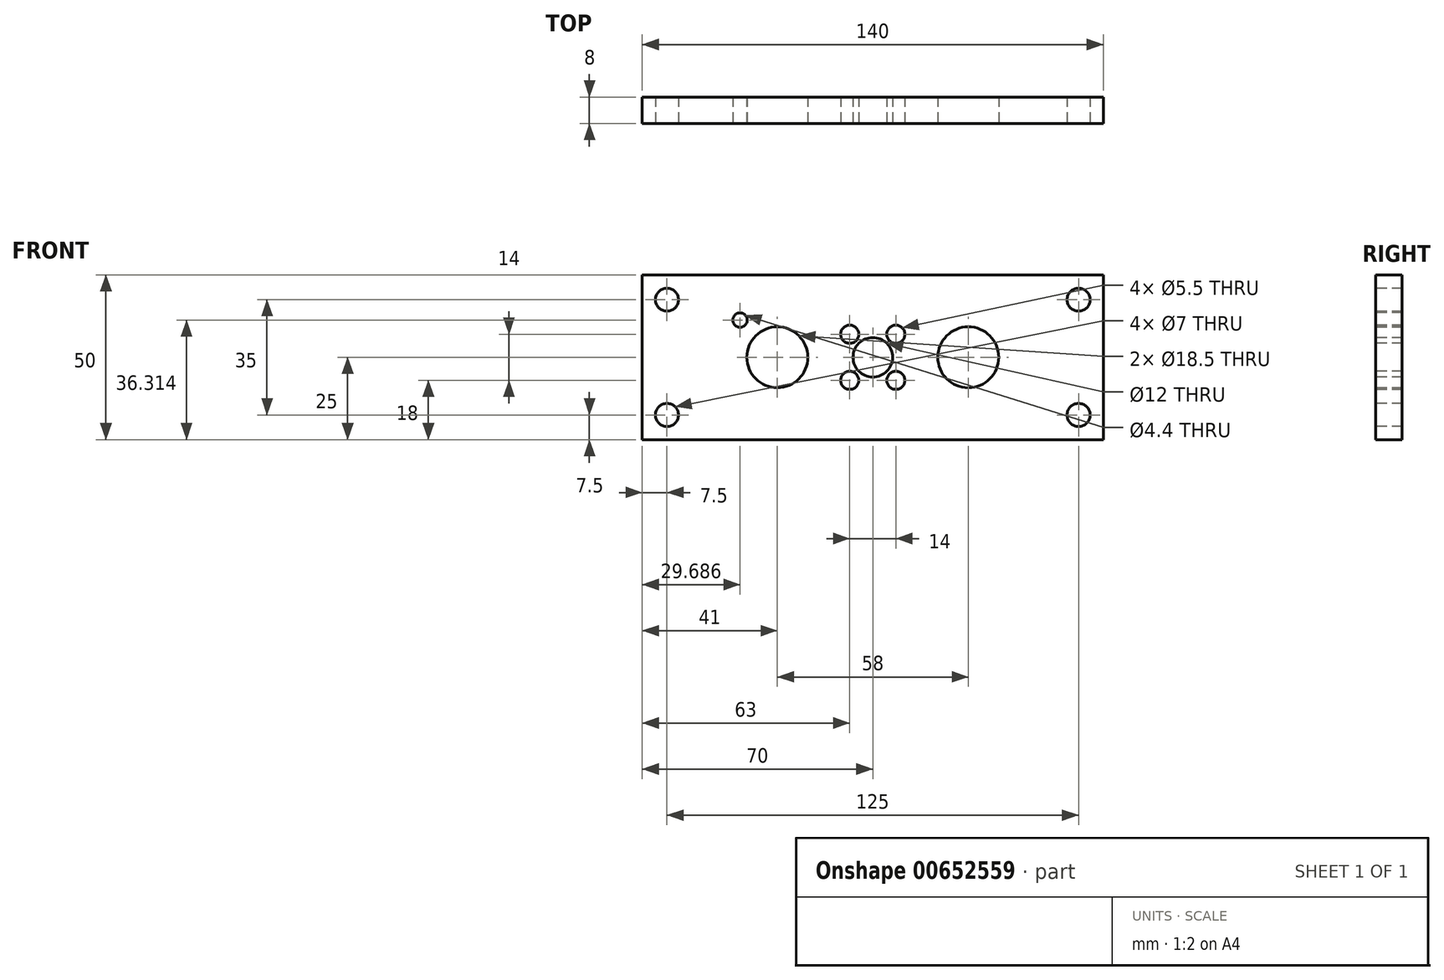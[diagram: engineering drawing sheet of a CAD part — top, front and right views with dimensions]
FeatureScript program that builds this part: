
annotation { "Feature Type Name" : "Feature", "Feature Type Description" : "" }
export const myFeature = defineFeature(function(context is Context, id is Id, definition is map)
    precondition{}
    {
        {
            var Q0;
            Q0=qCreatedBy(makeId("Front.planeOp"),FACE);
            var sketch = newSketch(context, id + "F0", { "sketchPlane" : qUnion([Q0])});
            skLineSegment(sketch, "E0.bottom", {"start": v(70, 25) * mm, "end": v(-70, 25) * mm});
            skLineSegment(sketch, "E0.top", {"start": v(70, -25) * mm, "end": v(-70, -25) * mm});
            skLineSegment(sketch, "E0.left", {"start": v(70, 25) * mm, "end": v(70, -25) * mm});
            skLineSegment(sketch, "E0.right", {"start": v(-70, 25) * mm, "end": v(-70, -25) * mm});
            skPoint(sketch, "E0.middle", {"position": v(0, 0) * mm});
            skSolve(sketch);
        }
        {
            var Q0;
            Q0=makeQuery(id+"F0.imprint","IMPRINT",FACE,{"disambiguationData":[TD([[makeQuery(id+"F0.imprint","IMPRINT",EDGE,{"derivedFrom":sQuery(id+"F0.wireOp",EDGE,"E0.bottom")}),1.0]])]});
            extrude(context, id + "F1", {"entities" : qUnion([Q0]), "depth" : 8 * mm, "offsetDistance" : 25 * mm});
        }
        {
            var Q0;
            Q0=makeQuery(id+"F1.opExtrude","CAP_FACE",FACE,{"disambiguationData":[OSD([sQuery(id+"F0.wireOp",EDGE,"E0.bottom"),sQuery(id+"F0.wireOp",EDGE,"E0.top"),sQuery(id+"F0.wireOp",EDGE,"E0.left"),sQuery(id+"F0.wireOp",EDGE,"E0.right")])],"isStart":false});
            var sketch = newSketch(context, id + "F2", { "sketchPlane" : qUnion([Q0])});
            skPoint(sketch, "E1", {"position": v(-62.5, 17.5) * mm});
            skPoint(sketch, "E2", {"position": v(-62.5, -17.5) * mm});
            skPoint(sketch, "E3", {"position": v(62.5, 17.5) * mm});
            skPoint(sketch, "E4", {"position": v(62.5, -17.5) * mm});
            skPoint(sketch, "E5", {"position": v(-29, 0) * mm});
            skPoint(sketch, "E6", {"position": v(29, 0) * mm});
            skPoint(sketch, "E7", {"position": v(0, 0) * mm});
            skPoint(sketch, "E8", {"position": v(7, -7) * mm});
            skPoint(sketch, "E9", {"position": v(-7, 7) * mm});
            skPoint(sketch, "E10", {"position": v(7, 7) * mm});
            skPoint(sketch, "E11", {"position": v(-7, -7) * mm});
            skLineSegment(sketch, "E12", {"start": v(-29, 0) * mm, "end": v(-40.31, 11.31) * mm});
            skSolve(sketch);
        }
        {
            var Q0;
            Q0=sQuery(id+"F2.wireOp",VERTEX,"E7");
            var Q1;
            Q1=makeQuery(id+"F1.opExtrude","SWEPT_BODY",BODY,{"disambiguationData":[OSD([sQuery(id+"F0.wireOp",EDGE,"E0.bottom"),sQuery(id+"F0.wireOp",EDGE,"E0.top"),sQuery(id+"F0.wireOp",EDGE,"E0.left"),sQuery(id+"F0.wireOp",EDGE,"E0.right")])]});
            hole(context, id + "F3", {"style" : HoleStyle.SIMPLE, "endStyle" : HoleEndStyle.THROUGH, "holeDiameter" : 12 * mm, "majorDiameter" : 5 * mm, "isTappedThrough" : true, "tappedDepth" : 12 * mm, "tapClearance" : 3, "locations" : qUnion([Q0]), "scope" : qUnion([Q1])});
        }
        {
            var Q0;
            Q0=sQuery(id+"F2.wireOp",VERTEX,"E9");
            var Q1;
            Q1=sQuery(id+"F2.wireOp",VERTEX,"E11");
            var Q2;
            Q2=sQuery(id+"F2.wireOp",VERTEX,"E8");
            var Q3;
            Q3=sQuery(id+"F2.wireOp",VERTEX,"E10");
            var Q4;
            Q4=makeQuery(id+"F1.opExtrude","SWEPT_BODY",BODY,{"disambiguationData":[OSD([sQuery(id+"F0.wireOp",EDGE,"E0.bottom"),sQuery(id+"F0.wireOp",EDGE,"E0.top"),sQuery(id+"F0.wireOp",EDGE,"E0.left"),sQuery(id+"F0.wireOp",EDGE,"E0.right")])]});
            hole(context, id + "F4", {"style" : HoleStyle.SIMPLE, "endStyle" : HoleEndStyle.THROUGH, "holeDiameter" : 5.5 * mm, "majorDiameter" : 5 * mm, "isTappedThrough" : true, "tappedDepth" : 12 * mm, "tapClearance" : 3, "locations" : qUnion([Q0, Q1, Q2, Q3]), "scope" : qUnion([Q4])});
        }
        {
            var Q0;
            Q0=sQuery(id+"F2.wireOp",VERTEX,"E2");
            var Q1;
            Q1=sQuery(id+"F2.wireOp",VERTEX,"E4");
            var Q2;
            Q2=sQuery(id+"F2.wireOp",VERTEX,"E3");
            var Q3;
            Q3=sQuery(id+"F2.wireOp",VERTEX,"E1");
            var Q4;
            Q4=makeQuery(id+"F1.opExtrude","SWEPT_BODY",BODY,{"disambiguationData":[OSD([sQuery(id+"F0.wireOp",EDGE,"E0.bottom"),sQuery(id+"F0.wireOp",EDGE,"E0.top"),sQuery(id+"F0.wireOp",EDGE,"E0.left"),sQuery(id+"F0.wireOp",EDGE,"E0.right")])]});
            hole(context, id + "F5", {"style" : HoleStyle.SIMPLE, "endStyle" : HoleEndStyle.THROUGH, "holeDiameter" : 7 * mm, "majorDiameter" : 5 * mm, "isTappedThrough" : true, "tappedDepth" : 12 * mm, "tapClearance" : 3, "locations" : qUnion([Q0, Q1, Q2, Q3]), "scope" : qUnion([Q4])});
        }
        {
            var Q0;
            Q0=sQuery(id+"F2.wireOp",VERTEX,"E5");
            var Q1;
            Q1=sQuery(id+"F2.wireOp",VERTEX,"E6");
            var Q2;
            Q2=makeQuery(id+"F1.opExtrude","SWEPT_BODY",BODY,{"disambiguationData":[OSD([sQuery(id+"F0.wireOp",EDGE,"E0.bottom"),sQuery(id+"F0.wireOp",EDGE,"E0.top"),sQuery(id+"F0.wireOp",EDGE,"E0.left"),sQuery(id+"F0.wireOp",EDGE,"E0.right")])]});
            hole(context, id + "F6", {"style" : HoleStyle.SIMPLE, "endStyle" : HoleEndStyle.THROUGH, "holeDiameter" : 18.5 * mm, "majorDiameter" : 5 * mm, "isTappedThrough" : true, "tappedDepth" : 12 * mm, "tapClearance" : 3, "locations" : qUnion([Q0, Q1]), "scope" : qUnion([Q2])});
        }
        {
            var Q0;
            Q0=sQuery(id+"F2.wireOp",VERTEX,"E12.end");
            var Q1;
            Q1=makeQuery(id+"F1.opExtrude","SWEPT_BODY",BODY,{"disambiguationData":[OSD([sQuery(id+"F0.wireOp",EDGE,"E0.bottom"),sQuery(id+"F0.wireOp",EDGE,"E0.top"),sQuery(id+"F0.wireOp",EDGE,"E0.left"),sQuery(id+"F0.wireOp",EDGE,"E0.right")])]});
            hole(context, id + "F7", {"style" : HoleStyle.SIMPLE, "endStyle" : HoleEndStyle.THROUGH, "standardTappedOrClearance" : lookupTablePath({ "standard" : "ISO", "fit" : "Normal", "size" : "M4", "type" : "Clearance" }), "standardBlindInLast" : lookupTablePath({ "fit" : "Standard", "standard" : "ISO", "size" : "M4", "type" : "Clearance" }), "holeDiameter" : 4.4 * mm, "majorDiameter" : 5 * mm, "isTappedThrough" : true, "tappedDepth" : 12 * mm, "tapClearance" : 3, "locations" : qUnion([Q0]), "scope" : qUnion([Q1])});
        }
    });
